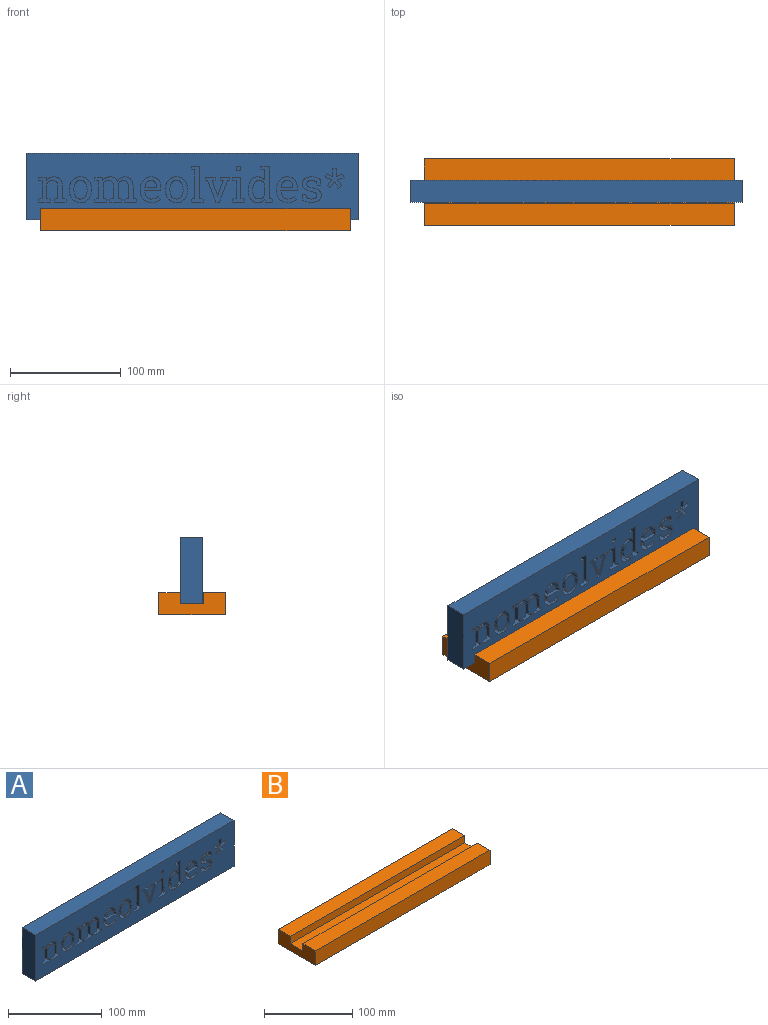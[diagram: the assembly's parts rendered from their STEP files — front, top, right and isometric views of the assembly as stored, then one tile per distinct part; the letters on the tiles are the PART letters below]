
ASSEMBLY  parts=2 mates=1
PART A: 294 faces, bbox 300x20x60 mm
  f0: plane 300x60mm, normal (0,-1,0), area 14784.2mm2, adj f1,f2,f3,f4,f6,f7,f8,f9
  f1: plane 60x20mm, normal (-1,0,0), area 1200mm2, adj f0,f2,f4,f5
  f2: plane 300x20mm, normal (0,0,-1), area 6000mm2, adj f0,f1,f3,f5
  f3: plane 60x20mm, normal (1,0,0), area 1200mm2, adj f0,f2,f4,f5
  f4: plane 300x20mm, normal (0,0,1), area 6000mm2, adj f0,f1,f3,f5
  f5: plane 300x60mm, normal (0,1,0), area 18000mm2, adj f1,f2,f3,f4
  f6: plane 15x4.17mm, normal (-1,0,0), area 62.5mm2, adj f0,f7,f9,f10
  f7: plane 15x4.08mm, normal (0,0,-1), area 61.2mm2, adj f0,f6,f8,f10
  f8: plane 15x4.17mm, normal (1,0,0), area 62.5mm2, adj f0,f7,f9,f10
  f9: plane 15x4.08mm, normal (0,0,1), area 61.2mm2, adj f0,f6,f8,f10
  f10: plane 4.17x4.08mm, normal (0,-1,0), area 17mm2, adj f6,f7,f8,f9
  f11: plane 15x4.96mm, normal (-1,0,-0.04), area 74.4mm2, adj f0,f12,f40,f41
  f12: extruded ~15x3.38mm, area 58.1mm2, adj f0,f11,f13,f41
  f13: extruded ~15x4.58mm, area 69.8mm2, adj f0,f12,f14,f41
  f14: extruded ~15x6.06mm, area 97.4mm2, adj f0,f13,f15,f41
  f15: extruded ~15x4.67mm, area 81mm2, adj f0,f14,f16,f41
  f16: extruded ~15x4.15mm, area 72.4mm2, adj f0,f15,f17,f41
  f17: extruded ~15x6.15mm, area 99.9mm2, adj f0,f16,f18,f41
  f18: extruded ~15x3.89mm, area 63.1mm2, adj f0,f17,f19,f41
  f19: extruded ~15x2.22mm, area 37.9mm2, adj f0,f18,f20,f41
  f20: extruded ~15x2.31mm, area 41mm2, adj f0,f19,f21,f41
  f21: extruded ~15x3.41mm, area 53.7mm2, adj f0,f20,f22,f41
  f22: extruded ~15x2.48mm, area 37.5mm2, adj f0,f21,f23,f41
  f23: extruded ~15x1.91mm, area 32.3mm2, adj f0,f22,f24,f41
  f24: plane 15x3mm, normal (-0.97,0,-0.25), area 46.5mm2, adj f0,f23,f25,f41
  f25: plane 15x3.07mm, normal (0,0,-1), area 46.1mm2, adj f0,f24,f26,f41
  f26: plane 15x5.12mm, normal (1,0,0.01), area 76.8mm2, adj f0,f25,f27,f41
  f27: extruded ~15x3.63mm, area 60.4mm2, adj f0,f26,f28,f41
  f28: extruded ~15x4.58mm, area 69.5mm2, adj f0,f27,f29,f41
  f29: extruded ~15x6.31mm, area 100.5mm2, adj f0,f28,f30,f41
  f30: extruded ~15x4.83mm, area 84.2mm2, adj f0,f29,f31,f41
  f31: extruded ~15x4.2mm, area 73mm2, adj f0,f30,f32,f41
  f32: extruded ~15x6.32mm, area 102.6mm2, adj f0,f31,f33,f41
  f33: extruded ~15x3.79mm, area 60.9mm2, adj f0,f32,f34,f41
  f34: extruded ~15x2.09mm, area 35.6mm2, adj f0,f33,f35,f41
  f35: extruded ~15x2.3mm, area 39.1mm2, adj f0,f34,f36,f41
  f36: extruded ~15x3.23mm, area 51.7mm2, adj f0,f35,f37,f41
  f37: extruded ~15x2.56mm, area 39.2mm2, adj f0,f36,f38,f41
  f38: extruded ~15x1.87mm, area 33mm2, adj f0,f37,f39,f41
  f39: plane 15x2.69mm, normal (0.97,0,0.24), area 41.6mm2, adj f0,f38,f40,f41
  f40: plane 15x3.07mm, normal (0,0,1), area 46.1mm2, adj f0,f11,f39,f41
  f41: plane 23.28x17.23mm, normal (0,-1,0), area 203.8mm2, adj f11,f12,f13,f14,f15,f16,f17,f18
  f42: plane 15x5.68mm, normal (0.81,0,-0.59), area 105mm2, adj f0,f43,f56,f57
  f43: plane 15x2.73mm, normal (0.58,0,0.82), area 50.2mm2, adj f0,f42,f44,f57
  f44: plane 15x5.78mm, normal (-0.85,0,0.53), area 102.6mm2, adj f0,f43,f45,f57
  f45: plane 15x5.95mm, normal (0.85,0,0.53), area 105.5mm2, adj f0,f44,f46,f57
  f46: plane 15x2.71mm, normal (-0.59,0,0.81), area 50.5mm2, adj f0,f45,f47,f57
  f47: plane 15x5.6mm, normal (-0.81,0,-0.58), area 103.2mm2, adj f0,f46,f48,f57
  f48: plane 15x6.26mm, normal (-0.28,0,0.96), area 97.9mm2, adj f0,f47,f49,f57
  f49: plane 15x3.23mm, normal (-0.96,0,-0.29), area 50.7mm2, adj f0,f48,f50,f57
  f50: plane 15x6.08mm, normal (0.35,0,-0.94), area 97.3mm2, adj f0,f49,f51,f57
  f51: plane 15x7.21mm, normal (-1,0,0.03), area 108.2mm2, adj f0,f50,f52,f57
  f52: plane 15x3.34mm, normal (0,0,-1), area 50mm2, adj f0,f51,f53,f57
  f53: plane 15x7.09mm, normal (1,0,0.03), area 106.4mm2, adj f0,f52,f54,f57
  f54: plane 15x6.14mm, normal (-0.35,0,-0.94), area 98.3mm2, adj f0,f53,f55,f57
  f55: plane 15x3.19mm, normal (0.95,0,-0.3), area 50.2mm2, adj f0,f54,f56,f57
  f56: plane 15x6.14mm, normal (0.29,0,0.96), area 96.1mm2, adj f0,f42,f55,f57
  f57: plane 17.6x17.15mm, normal (0,-1,0), area 121.5mm2, adj f42,f43,f44,f45,f46,f47,f48,f49
  f58: plane 15x0.46mm, normal (1,0,0), area 6.9mm2, adj f0,f59,f77,f78
  f59: extruded ~15x8.2mm, area 132.2mm2, adj f0,f58,f60,f78
  f60: extruded ~15x7.36mm, area 124.6mm2, adj f0,f59,f61,f78
  f61: extruded ~15x7.32mm, area 123.9mm2, adj f0,f60,f62,f78
  f62: extruded ~15x8.21mm, area 132.4mm2, adj f0,f61,f63,f78
  f63: plane 15x0.46mm, normal (-1,0,0), area 6.9mm2, adj f0,f62,f64,f78
  f64: extruded ~15x8.21mm, area 132.4mm2, adj f0,f63,f65,f78
  f65: extruded ~15x7.35mm, area 124.5mm2, adj f0,f64,f66,f78
  f66: extruded ~15x7.32mm, area 124.2mm2, adj f0,f65,f77,f78
  f67: plane 15x0.46mm, normal (-1,0,0), area 6.9mm2, adj f68,f76,f78,f79
  f68: extruded ~15x5.86mm, area 92mm2, adj f67,f69,f78,f79
  f69: extruded ~15x4.44mm, area 78.9mm2, adj f68,f70,f78,f79
  f70: extruded ~15x4.45mm, area 79mm2, adj f69,f71,f78,f79
  f71: extruded ~15x5.86mm, area 92.1mm2, adj f70,f72,f78,f79
  f72: plane 15x0.46mm, normal (1,0,0), area 6.9mm2, adj f71,f73,f78,f79
  f73: extruded ~15x5.88mm, area 92.4mm2, adj f72,f74,f78,f79
  f74: extruded ~15x4.41mm, area 78.3mm2, adj f73,f75,f78,f79
  f75: extruded ~15x4.47mm, area 79.1mm2, adj f74,f76,f78,f79
  f76: extruded ~15x5.88mm, area 92.4mm2, adj f67,f75,f78,f79
  f77: extruded ~15x8.2mm, area 132.2mm2, adj f0,f58,f66,f78
  f78: plane 23.28x20.07mm, normal (0,-1,0), area 214.5mm2, adj f58,f59,f60,f61,f62,f63,f64,f65
  f79: plane 16.87x11.9mm, normal (0,-1,0), area 164.5mm2, adj f67,f68,f69,f70,f71,f72,f73,f74
  f80: plane 15x2.61mm, normal (1,0,0), area 39.2mm2, adj f0,f81,f89,f90
  f81: plane 15x10.85mm, normal (0,0,1), area 162.7mm2, adj f0,f80,f82,f90
  f82: plane 15x2.61mm, normal (-1,0,0), area 39.2mm2, adj f0,f81,f83,f90
  f83: plane 15x3.38mm, normal (-0.17,0,-0.99), area 51.5mm2, adj f0,f82,f84,f90
  f84: plane 19.24x15mm, normal (-1,0,0), area 288.5mm2, adj f0,f83,f85,f90
  f85: plane 15x7.46mm, normal (0,0,-1), area 111.9mm2, adj f0,f84,f86,f90
  f86: plane 15x2.63mm, normal (1,0,0), area 39.5mm2, adj f0,f85,f87,f90
  f87: plane 15x3.38mm, normal (0.17,0,0.99), area 51.5mm2, adj f0,f86,f88,f90
  f88: plane 16.03x15mm, normal (1,0,0), area 240.4mm2, adj f0,f87,f89,f90
  f89: plane 15x3.38mm, normal (0.17,0,-0.99), area 51.5mm2, adj f0,f80,f88,f90
  f90: plane 22.43x10.85mm, normal (0,-1,0), area 121mm2, adj f80,f81,f82,f83,f84,f85,f86,f87
  f91: plane 15x2.63mm, normal (-1,0,0), area 39.5mm2, adj f0,f92,f108,f109
  f92: plane 15x8.67mm, normal (0,0,-1), area 130mm2, adj f0,f91,f93,f109
  f93: plane 15x2.63mm, normal (1,0,0), area 39.5mm2, adj f0,f92,f94,f109
  f94: plane 15x1.84mm, normal (0.16,0,0.99), area 28mm2, adj f0,f93,f95,f109
  f95: plane 19.49x15mm, normal (0.93,0,0.36), area 313.8mm2, adj f0,f94,f96,f109
  f96: plane 15x3.09mm, normal (0,0,1), area 46.4mm2, adj f0,f95,f97,f109
  f97: plane 19.49x15mm, normal (-0.93,0,0.36), area 313.3mm2, adj f0,f96,f98,f109
  f98: plane 15x1.84mm, normal (-0.16,0,0.99), area 28mm2, adj f0,f97,f99,f109
  f99: plane 15x2.63mm, normal (-1,0,0), area 39.5mm2, adj f0,f98,f100,f109
  f100: plane 15x8.66mm, normal (0,0,-1), area 129.9mm2, adj f0,f99,f101,f109
  f101: plane 15x2.63mm, normal (1,0,0), area 39.5mm2, adj f0,f100,f102,f109
  f102: plane 15x2.72mm, normal (0.15,0,0.99), area 41.3mm2, adj f0,f101,f103,f109
  f103: plane 15x12.77mm, normal (0.94,0,-0.33), area 203mm2, adj f0,f102,f104,f109
  f104: plane 15x1.62mm, normal (0.97,0,-0.24), area 25mm2, adj f0,f103,f105,f109
  f105: plane 15x0.13mm, normal (0,0,-1), area 1.9mm2, adj f0,f104,f106,f109
  f106: plane 15x1.62mm, normal (-0.97,0,-0.22), area 24.9mm2, adj f0,f105,f107,f109
  f107: plane 15x12.77mm, normal (-0.94,0,-0.34), area 203.7mm2, adj f0,f106,f108,f109
  f108: plane 15x2.7mm, normal (-0.15,0,0.99), area 41mm2, adj f0,f91,f107,f109
  f109: plane 22.43x21.91mm, normal (0,-1,0), area 186.1mm2, adj f91,f92,f93,f94,f95,f96,f97,f98
  f110: plane 15x3.38mm, normal (0.17,0,0.99), area 51.4mm2, adj f0,f111,f119,f120
  f111: plane 25.94x15mm, normal (1,0,0), area 389mm2, adj f0,f110,f112,f120
  f112: plane 15x3.38mm, normal (0.17,0,-0.99), area 51.4mm2, adj f0,f111,f113,f120
  f113: plane 15x2.61mm, normal (1,0,0), area 39.2mm2, adj f0,f112,f114,f120
  f114: plane 15x10.84mm, normal (0,0,1), area 162.6mm2, adj f0,f113,f115,f120
  f115: plane 15x2.61mm, normal (-1,0,0), area 39.2mm2, adj f0,f114,f116,f120
  f116: plane 15x3.38mm, normal (-0.17,0,-0.99), area 51.4mm2, adj f0,f115,f117,f120
  f117: plane 29.15x15mm, normal (-1,0,0), area 437.2mm2, adj f0,f116,f118,f120
  f118: plane 15x7.46mm, normal (0,0,-1), area 111.9mm2, adj f0,f117,f119,f120
  f119: plane 15x2.63mm, normal (1,0,0), area 39.5mm2, adj f0,f110,f118,f120
  f120: plane 32.34x10.84mm, normal (0,-1,0), area 161.6mm2, adj f110,f111,f112,f113,f114,f115,f116,f117
  f121: plane 15x2.61mm, normal (1,0,0), area 39.2mm2, adj f0,f122,f161,f162
  f122: plane 15x10.85mm, normal (0,0,1), area 162.7mm2, adj f0,f121,f123,f162
  f123: plane 15x2.61mm, normal (-1,0,0), area 39.2mm2, adj f0,f122,f124,f162
  f124: plane 15x3.38mm, normal (-0.17,0,-0.99), area 51.5mm2, adj f0,f123,f125,f162
  f125: plane 15x13.41mm, normal (-1,0,0), area 201.2mm2, adj f0,f124,f126,f162
  f126: extruded ~15x2.16mm, area 43.2mm2, adj f0,f125,f127,f162
  f127: extruded ~15x3.07mm, area 48.1mm2, adj f0,f126,f128,f162
  f128: extruded ~15x3.39mm, area 57.4mm2, adj f0,f127,f129,f162
  f129: extruded ~15x4.61mm, area 72.7mm2, adj f0,f128,f130,f162
  f130: plane 15x10.26mm, normal (1,0,0), area 153.9mm2, adj f0,f129,f131,f162
  f131: plane 15x3.38mm, normal (0.17,0,-0.99), area 51.4mm2, adj f0,f130,f132,f162
  f132: plane 15x2.61mm, normal (1,0,0), area 39.2mm2, adj f0,f131,f133,f162
  f133: plane 15x10.84mm, normal (0,0,1), area 162.6mm2, adj f0,f132,f134,f162
  f134: plane 15x2.61mm, normal (-1,0,0), area 39.2mm2, adj f0,f133,f135,f162
  f135: plane 15x3.38mm, normal (-0.17,0,-0.99), area 51.4mm2, adj f0,f134,f136,f162
  f136: plane 15x11.05mm, normal (-1,0,0), area 165.8mm2, adj f0,f135,f137,f162
  f137: extruded ~15x3.78mm, area 62.1mm2, adj f0,f136,f138,f162
  f138: extruded ~15x3.43mm, area 58.1mm2, adj f0,f137,f139,f162
  f139: extruded ~15x3.38mm, area 56.6mm2, adj f0,f138,f140,f162
  f140: extruded ~15x4.7mm, area 73.8mm2, adj f0,f139,f141,f162
  f141: plane 15x10.26mm, normal (1,0,0), area 153.9mm2, adj f0,f140,f142,f162
  f142: plane 15x3.38mm, normal (0.17,0,-0.99), area 51.4mm2, adj f0,f141,f143,f162
  f143: plane 15x2.61mm, normal (1,0,0), area 39.2mm2, adj f0,f142,f144,f162
  f144: plane 15x10.86mm, normal (0,0,1), area 162.9mm2, adj f0,f143,f145,f162
  f145: plane 15x2.61mm, normal (-1,0,0), area 39.2mm2, adj f0,f144,f146,f162
  f146: plane 15x3.38mm, normal (-0.17,0,-0.99), area 51.4mm2, adj f0,f145,f147,f162
  f147: plane 15x10.22mm, normal (-1,0,0), area 153.3mm2, adj f0,f146,f148,f162
  f148: extruded ~15x7.08mm, area 112.5mm2, adj f0,f147,f149,f162
  f149: extruded ~15x5.43mm, area 91.9mm2, adj f0,f148,f150,f162
  f150: extruded ~15x4.06mm, area 64.1mm2, adj f0,f149,f151,f162
  f151: extruded ~15x3.02mm, area 62.4mm2, adj f0,f150,f152,f162
  f152: extruded ~15x3.11mm, area 60.1mm2, adj f0,f151,f153,f162
  f153: extruded ~15x3.84mm, area 60.6mm2, adj f0,f152,f154,f162
  f154: extruded ~15x3.94mm, area 61.1mm2, adj f0,f153,f155,f162
  f155: extruded ~15x2.78mm, area 56.3mm2, adj f0,f154,f156,f162
  f156: plane 15x2.92mm, normal (-1,0,-0.09), area 44mm2, adj f0,f155,f157,f162
  f157: plane 15x7.05mm, normal (0,0,-1), area 105.8mm2, adj f0,f156,f158,f162
  f158: plane 15x2.63mm, normal (1,0,0), area 39.5mm2, adj f0,f157,f159,f162
  f159: plane 15x3.38mm, normal (0.17,0,0.99), area 51.5mm2, adj f0,f158,f160,f162
  f160: plane 16.03x15mm, normal (1,0,0), area 240.4mm2, adj f0,f159,f161,f162
  f161: plane 15x3.38mm, normal (0.17,0,-0.99), area 51.5mm2, adj f0,f121,f160,f162
  f162: plane 37.95x22.84mm, normal (0,-1,0), area 394.7mm2, adj f121,f122,f123,f124,f125,f126,f127,f128
  f163: extruded ~15x4.76mm, area 72.8mm2, adj f0,f164,f186,f187
  f164: extruded ~15x3.18mm, area 56.4mm2, adj f0,f163,f165,f187
  f165: plane 15x2.65mm, normal (-0.86,0,-0.52), area 46.5mm2, adj f0,f164,f166,f187
  f166: extruded ~15x2.71mm, area 47.6mm2, adj f0,f165,f167,f187
  f167: extruded ~15x3.64mm, area 55.5mm2, adj f0,f166,f168,f187
  f168: extruded ~15x4.41mm, area 76.1mm2, adj f0,f167,f169,f187
  f169: extruded ~15x5.31mm, area 84.8mm2, adj f0,f168,f170,f187
  f170: plane 15x0.11mm, normal (-0.85,0,0.53), area 1.9mm2, adj f0,f169,f171,f187
  f171: plane 15x14.55mm, normal (0,0,1), area 218.3mm2, adj f0,f170,f172,f187
  f172: plane 15x2.55mm, normal (-1,0,0), area 38.2mm2, adj f0,f171,f173,f187
  f173: extruded ~15x7.3mm, area 117.5mm2, adj f0,f172,f174,f187
  f174: extruded ~15x6.85mm, area 114.4mm2, adj f0,f173,f175,f187
  f175: extruded ~15x6.75mm, area 115.5mm2, adj f0,f174,f176,f187
  f176: extruded ~15x7.97mm, area 129.9mm2, adj f0,f175,f177,f187
  f177: plane 15x0.92mm, normal (1,0,0), area 13.7mm2, adj f0,f176,f178,f187
  f178: extruded ~15x8.1mm, area 131.3mm2, adj f0,f177,f186,f187
  f179: extruded ~15x3.81mm, area 64.4mm2, adj f180,f185,f187,f188
  f180: extruded ~15x4.02mm, area 64.6mm2, adj f179,f181,f187,f188
  f181: plane 15x0.54mm, normal (1,0,0), area 8.1mm2, adj f180,f182,f187,f188
  f182: plane 15x10.34mm, normal (0,0,-1), area 155.1mm2, adj f181,f183,f187,f188
  f183: plane 15x0.11mm, normal (-0.92,0,-0.4), area 1.7mm2, adj f182,f184,f187,f188
  f184: extruded ~15x4.34mm, area 71.4mm2, adj f183,f185,f187,f188
  f185: extruded ~15x3.5mm, area 60.6mm2, adj f179,f184,f187,f188
  f186: extruded ~15x7.45mm, area 125.1mm2, adj f0,f163,f178,f187
  f187: plane 23.28x18.78mm, normal (0,-1,0), area 221.4mm2, adj f163,f164,f165,f166,f167,f168,f169,f170
  f188: plane 10.39x6.18mm, normal (0,-1,0), area 51.1mm2, adj f179,f180,f181,f182,f183,f184,f185
  f189: plane 15x0.46mm, normal (1,0,0), area 6.9mm2, adj f0,f190,f208,f209
  f190: extruded ~15x8.2mm, area 132.2mm2, adj f0,f189,f191,f209
  f191: extruded ~15x7.36mm, area 124.6mm2, adj f0,f190,f192,f209
  f192: extruded ~15x7.32mm, area 123.9mm2, adj f0,f191,f193,f209
  f193: extruded ~15x8.21mm, area 132.4mm2, adj f0,f192,f194,f209
  f194: plane 15x0.46mm, normal (-1,0,0), area 6.9mm2, adj f0,f193,f195,f209
  f195: extruded ~15x8.21mm, area 132.4mm2, adj f0,f194,f196,f209
  f196: extruded ~15x7.35mm, area 124.5mm2, adj f0,f195,f197,f209
  f197: extruded ~15x7.32mm, area 124.2mm2, adj f0,f196,f208,f209
  f198: plane 15x0.46mm, normal (-1,0,0), area 6.9mm2, adj f199,f207,f209,f210
  f199: extruded ~15x5.86mm, area 92mm2, adj f198,f200,f209,f210
  f200: extruded ~15x4.44mm, area 78.9mm2, adj f199,f201,f209,f210
  f201: extruded ~15x4.45mm, area 79mm2, adj f200,f202,f209,f210
  f202: extruded ~15x5.86mm, area 92.1mm2, adj f201,f203,f209,f210
  f203: plane 15x0.46mm, normal (1,0,0), area 6.9mm2, adj f202,f204,f209,f210
  f204: extruded ~15x5.88mm, area 92.4mm2, adj f203,f205,f209,f210
  f205: extruded ~15x4.41mm, area 78.3mm2, adj f204,f206,f209,f210
  f206: extruded ~15x4.47mm, area 79.1mm2, adj f205,f207,f209,f210
  f207: extruded ~15x5.88mm, area 92.4mm2, adj f198,f206,f209,f210
  f208: extruded ~15x8.2mm, area 132.2mm2, adj f0,f189,f197,f209
  f209: plane 23.28x20.07mm, normal (0,-1,0), area 214.5mm2, adj f189,f190,f191,f192,f193,f194,f195,f196
  f210: plane 16.87x11.9mm, normal (0,-1,0), area 164.5mm2, adj f198,f199,f200,f201,f202,f203,f204,f205
  f211: plane 15x2.67mm, normal (0.99,0,0.12), area 40.4mm2, adj f0,f212,f238,f239
  f212: plane 15x6.93mm, normal (0,0,1), area 103.9mm2, adj f0,f211,f213,f239
  f213: plane 15x2.61mm, normal (-1,0,0), area 39.2mm2, adj f0,f212,f214,f239
  f214: plane 15x3.38mm, normal (-0.17,0,-0.99), area 51.4mm2, adj f0,f213,f215,f239
  f215: plane 29.15x15mm, normal (-1,0,0), area 437.2mm2, adj f0,f214,f216,f239
  f216: plane 15x7.46mm, normal (0,0,-1), area 111.9mm2, adj f0,f215,f217,f239
  f217: plane 15x2.63mm, normal (1,0,0), area 39.5mm2, adj f0,f216,f218,f239
  f218: plane 15x3.38mm, normal (0.17,0,0.99), area 51.4mm2, adj f0,f217,f219,f239
  f219: plane 15x9.14mm, normal (1,0,0), area 137.1mm2, adj f0,f218,f220,f239
  f220: extruded ~15x2.6mm, area 50.8mm2, adj f0,f219,f221,f239
  f221: extruded ~15x3.52mm, area 54.3mm2, adj f0,f220,f222,f239
  f222: extruded ~15x6.46mm, area 113.6mm2, adj f0,f221,f223,f239
  f223: extruded ~15x8.73mm, area 137.6mm2, adj f0,f222,f224,f239
  f224: plane 15x0.43mm, normal (1,0,0), area 6.5mm2, adj f0,f223,f225,f239
  f225: extruded ~15x7.83mm, area 124.8mm2, adj f0,f224,f226,f239
  f226: extruded ~15x6.42mm, area 110.2mm2, adj f0,f225,f227,f239
  f227: extruded ~15x3.68mm, area 57mm2, adj f0,f226,f238,f239
  f228: plane 15x0.43mm, normal (-1,0,0), area 6.5mm2, adj f229,f237,f239,f240
  f229: extruded ~15x6.3mm, area 98mm2, adj f228,f230,f239,f240
  f230: extruded ~15x4.32mm, area 78.2mm2, adj f229,f231,f239,f240
  f231: extruded ~15x3.03mm, area 47.8mm2, adj f230,f232,f239,f240
  f232: extruded ~15x2.24mm, area 46mm2, adj f231,f233,f239,f240
  f233: plane 15x10.4mm, normal (1,0,0), area 156mm2, adj f232,f234,f239,f240
  f234: extruded ~15x2.35mm, area 47.3mm2, adj f233,f235,f239,f240
  f235: extruded ~15x3.07mm, area 48.4mm2, adj f234,f236,f239,f240
  f236: extruded ~15x4.29mm, area 74.5mm2, adj f235,f237,f239,f240
  f237: extruded ~15x5.44mm, area 85.4mm2, adj f228,f236,f239,f240
  f238: extruded ~15x2.68mm, area 53.7mm2, adj f0,f211,f227,f239
  f239: plane 32.77x22.35mm, normal (0,-1,0), area 295.4mm2, adj f211,f212,f213,f214,f215,f216,f217,f218
  f240: plane 16.65x10.8mm, normal (0,-1,0), area 154.6mm2, adj f228,f229,f230,f231,f232,f233,f234,f235
  f241: extruded ~15x4.76mm, area 72.8mm2, adj f0,f242,f264,f265
  f242: extruded ~15x3.18mm, area 56.4mm2, adj f0,f241,f243,f265
  f243: plane 15x2.65mm, normal (-0.86,0,-0.52), area 46.5mm2, adj f0,f242,f244,f265
  f244: extruded ~15x2.71mm, area 47.6mm2, adj f0,f243,f245,f265
  f245: extruded ~15x3.64mm, area 55.5mm2, adj f0,f244,f246,f265
  f246: extruded ~15x4.41mm, area 76.1mm2, adj f0,f245,f247,f265
  f247: extruded ~15x5.31mm, area 84.8mm2, adj f0,f246,f248,f265
  f248: plane 15x0.11mm, normal (-0.85,0,0.53), area 1.9mm2, adj f0,f247,f249,f265
  f249: plane 15x14.55mm, normal (0,0,1), area 218.3mm2, adj f0,f248,f250,f265
  f250: plane 15x2.55mm, normal (-1,0,0), area 38.2mm2, adj f0,f249,f251,f265
  f251: extruded ~15x7.3mm, area 117.5mm2, adj f0,f250,f252,f265
  f252: extruded ~15x6.85mm, area 114.4mm2, adj f0,f251,f253,f265
  f253: extruded ~15x6.75mm, area 115.5mm2, adj f0,f252,f254,f265
  f254: extruded ~15x7.97mm, area 129.9mm2, adj f0,f253,f255,f265
  f255: plane 15x0.92mm, normal (1,0,0), area 13.7mm2, adj f0,f254,f256,f265
  f256: extruded ~15x8.1mm, area 131.3mm2, adj f0,f255,f264,f265
  f257: extruded ~15x3.81mm, area 64.4mm2, adj f258,f263,f265,f266
  f258: extruded ~15x4.02mm, area 64.6mm2, adj f257,f259,f265,f266
  f259: plane 15x0.54mm, normal (1,0,0), area 8.1mm2, adj f258,f260,f265,f266
  f260: plane 15x10.34mm, normal (0,0,-1), area 155.1mm2, adj f259,f261,f265,f266
  f261: plane 15x0.11mm, normal (-0.92,0,-0.4), area 1.7mm2, adj f260,f262,f265,f266
  f262: extruded ~15x4.34mm, area 71.4mm2, adj f261,f263,f265,f266
  f263: extruded ~15x3.5mm, area 60.6mm2, adj f257,f262,f265,f266
  f264: extruded ~15x7.45mm, area 125.1mm2, adj f0,f241,f256,f265
  f265: plane 23.28x18.78mm, normal (0,-1,0), area 221.4mm2, adj f241,f242,f243,f244,f245,f246,f247,f248
  f266: plane 10.39x6.18mm, normal (0,-1,0), area 51.1mm2, adj f257,f258,f259,f260,f261,f262,f263
  f267: plane 15x2.61mm, normal (1,0,0), area 39.2mm2, adj f0,f268,f292,f293
  f268: plane 15x10.84mm, normal (0,0,1), area 162.6mm2, adj f0,f267,f269,f293
  f269: plane 15x2.61mm, normal (-1,0,0), area 39.2mm2, adj f0,f268,f270,f293
  f270: plane 15x3.38mm, normal (-0.17,0,-0.99), area 51.4mm2, adj f0,f269,f271,f293
  f271: plane 15x13.17mm, normal (-1,0,0), area 197.5mm2, adj f0,f270,f272,f293
  f272: extruded ~15x2.32mm, area 48.1mm2, adj f0,f271,f273,f293
  f273: extruded ~15x3.12mm, area 49.1mm2, adj f0,f272,f274,f293
  f274: extruded ~15x3.58mm, area 58.5mm2, adj f0,f273,f275,f293
  f275: extruded ~15x4.21mm, area 67mm2, adj f0,f274,f276,f293
  f276: plane 15x10.88mm, normal (1,0,0), area 163.3mm2, adj f0,f275,f277,f293
  f277: plane 15x3.38mm, normal (0.17,0,-0.99), area 51.4mm2, adj f0,f276,f278,f293
  f278: plane 15x2.61mm, normal (1,0,0), area 39.2mm2, adj f0,f277,f279,f293
  f279: plane 15x10.84mm, normal (0,0,1), area 162.6mm2, adj f0,f278,f280,f293
  f280: plane 15x2.61mm, normal (-1,0,0), area 39.2mm2, adj f0,f279,f281,f293
  f281: plane 15x3.38mm, normal (-0.17,0,-0.99), area 51.4mm2, adj f0,f280,f282,f293
  f282: plane 15x10.96mm, normal (-1,0,0), area 164.5mm2, adj f0,f281,f283,f293
  f283: extruded ~15x6.56mm, area 105.3mm2, adj f0,f282,f284,f293
  f284: extruded ~15x5.62mm, area 92.8mm2, adj f0,f283,f285,f293
  f285: extruded ~15x3.85mm, area 60.3mm2, adj f0,f284,f286,f293
  f286: extruded ~15x2.81mm, area 59.7mm2, adj f0,f285,f287,f293
  f287: plane 15x3.34mm, normal (-1,0,-0.09), area 50.2mm2, adj f0,f286,f288,f293
  f288: plane 15x7.02mm, normal (0,0,-1), area 105.4mm2, adj f0,f287,f289,f293
  f289: plane 15x2.63mm, normal (1,0,0), area 39.5mm2, adj f0,f288,f290,f293
  f290: plane 15x3.38mm, normal (0.17,0,0.99), area 51.4mm2, adj f0,f289,f291,f293
  f291: plane 16.03x15mm, normal (1,0,0), area 240.4mm2, adj f0,f290,f292,f293
  f292: plane 15x3.38mm, normal (0.17,0,-0.99), area 51.4mm2, adj f0,f267,f291,f293
  f293: plane 24.95x22.84mm, normal (0,-1,0), area 257.2mm2, adj f267,f268,f269,f270,f271,f272,f273,f274
PART B: 10 faces, bbox 280x60x20 mm
  f0: plane 280x19.5mm, normal (0,0,1), area 5460mm2, adj f1,f2,f4,f8
  f1: plane 60x20mm, normal (-1,0,0), area 995mm2, adj f0,f2,f3,f5,f6,f7,f8,f9
  f2: plane 280x20mm, normal (0,1,0), area 5600mm2, adj f0,f1,f4,f6
  f3: plane 280x20mm, normal (0,-1,0), area 5600mm2, adj f1,f4,f5,f6
  f4: plane 60x20mm, normal (1,0,0), area 995mm2, adj f0,f2,f3,f5,f6,f7,f8,f9
  f5: plane 280x20mm, normal (0,0,1), area 5600mm2, adj f1,f3,f4,f7
  f6: plane 280x60mm, normal (0,0,-1), area 16800mm2, adj f1,f2,f3,f4
  f7: plane 280x10mm, normal (0,1,0), area 2800mm2, adj f1,f4,f5,f9
  f8: plane 280x10mm, normal (0,-1,0), area 2800mm2, adj f0,f1,f4,f9
  f9: plane 280x20.5mm, normal (0,0,1), area 5740mm2, adj f1,f4,f7,f8
PLACE A t=(17.02,-10.42,-60.26)mm
PLACE B t=(29.49,59.84,-70.26)mm
MATE planar A.f2 <-> B.f9  axis (0,0,-1) through (24.82,-20.42,-60.26)mm
